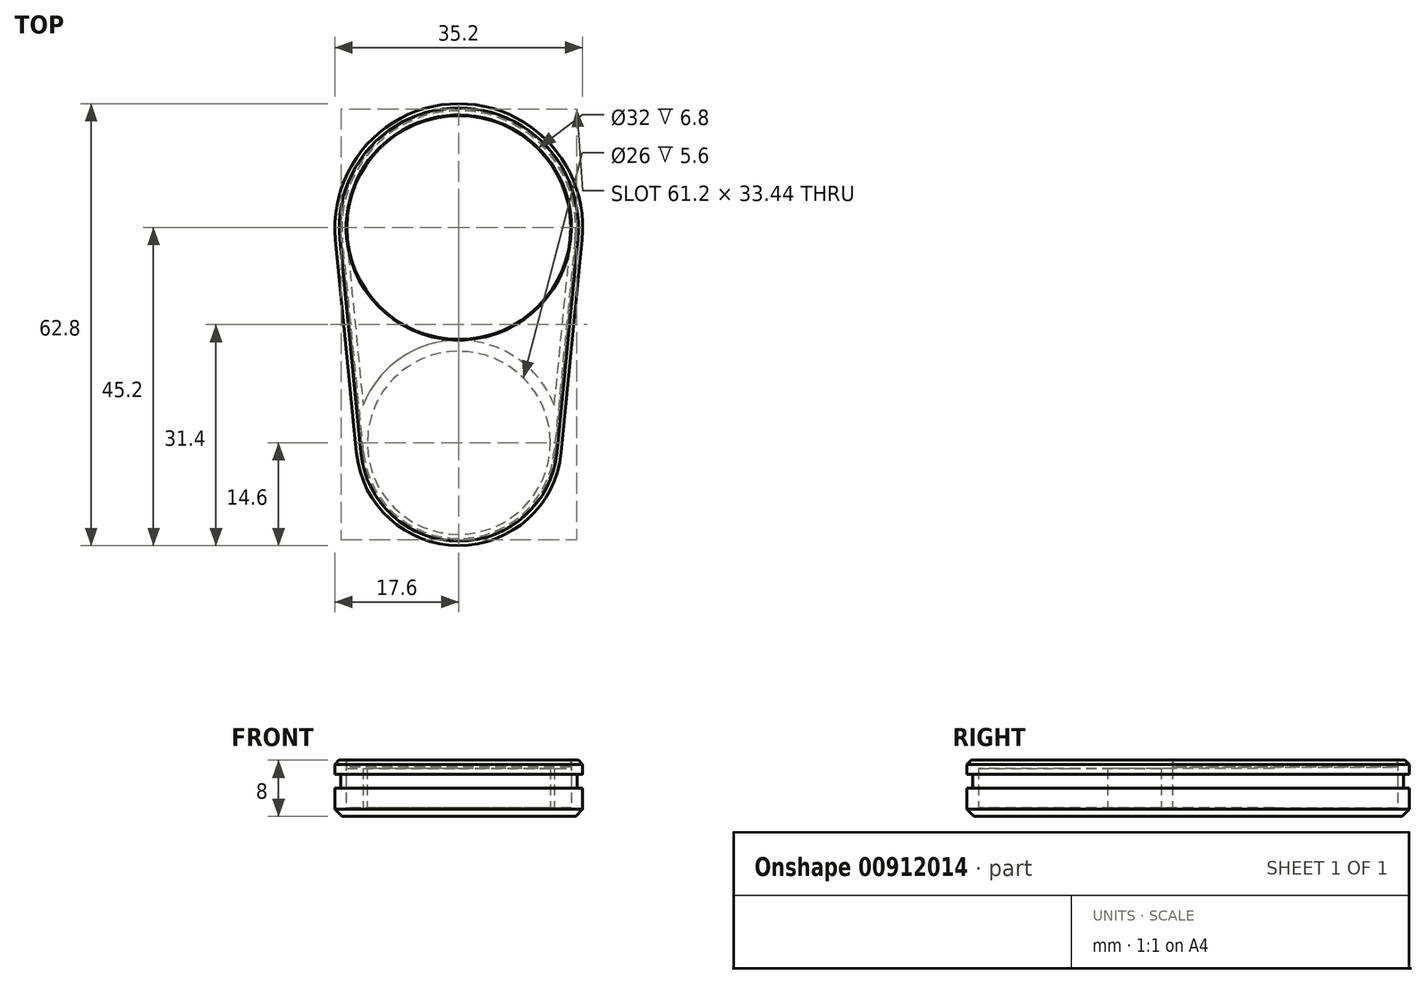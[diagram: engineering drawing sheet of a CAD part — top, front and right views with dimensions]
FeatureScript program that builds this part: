
annotation { "Feature Type Name" : "Feature", "Feature Type Description" : "" }
export const myFeature = defineFeature(function(context is Context, id is Id, definition is map)
    precondition{}
    {
        {
            var Q0;
            Q0=qCreatedBy(makeId("Top.planeOp"),FACE);
            var sketch = newSketch(context, id + "F0", { "sketchPlane" : qUnion([Q0])});
            skCircle(sketch, "E0", {"center": v(0, 0) * mm, "radius": 16 * mm});
            skCircle(sketch, "E1", {"center": v(0, 0) * mm, "radius": 17.6 * mm});
            skCircle(sketch, "E2", {"center": v(0, 0) * mm, "radius": 8.5 * mm});
            skCircle(sketch, "E3", {"center": v(0, 0) * mm, "radius": 7.3 * mm});
            skCircle(sketch, "E4", {"center": v(0, 0) * mm, "radius": 14 * mm});
            skLineSegment(sketch, "E5", {"start": v(0, 0) * mm, "end": v(0, -30.6) * mm, "construction": true});
            skCircle(sketch, "E6", {"center": v(0, -30.6) * mm, "radius": 13 * mm});
            skCircle(sketch, "E7", {"center": v(0, -30.6) * mm, "radius": 14.6 * mm});
            skLineSegment(sketch, "E8", {"start": v(14.53, -32.03) * mm, "end": v(17.69, 0) * mm});
            skLineSegment(sketch, "E9", {"start": v(-17.69, 0) * mm, "end": v(-14.53, -32.03) * mm});
            skLineSegment(sketch, "E10", {"start": v(-15.92, -1.57) * mm, "end": v(-12.94, -31.87) * mm});
            skLineSegment(sketch, "E11", {"start": v(12.94, -31.87) * mm, "end": v(15.92, -1.57) * mm});
            skSolve(sketch);
        }
        {
            var Q0;
            {var subQ0=sQuery(id+"F0.wireOp",EDGE,"E8");var subQ1=sQuery(id+"F0.wireOp",EDGE,"E1");var subQ2=makeQuery(id+"F0.imprint","INTERSECT",VERTEX,{"derivedFrom":[subQ1,subQ0]});Q0=makeQuery(id+"F0.imprint","IMPRINT",FACE,{"disambiguationData":[TD([[makeQuery(id+"F0.imprint","IMPRINT",EDGE,{"disambiguationData":[TD([[subQ2,1.0]])],"derivedFrom":subQ1}),-1.0]])]});}
            var Q1;
            {var subQ0=sQuery(id+"F0.wireOp",EDGE,"E7");var subQ1=sQuery(id+"F0.wireOp",EDGE,"E1");var subQ2=makeQuery(id+"F0.imprint","INTERSECT",VERTEX,{"disambiguationData":[OD(0.0)],"derivedFrom":[subQ1,subQ0]});Q1=makeQuery(id+"F0.imprint","IMPRINT",FACE,{"disambiguationData":[TD([[makeQuery(id+"F0.imprint","IMPRINT",EDGE,{"disambiguationData":[TD([[subQ2,-1.0]])],"derivedFrom":subQ1}),1.0]])]});}
            var Q2;
            {var subQ0=sQuery(id+"F0.wireOp",EDGE,"E11");var subQ1=sQuery(id+"F0.wireOp",EDGE,"E0");var subQ2=makeQuery(id+"F0.imprint","INTERSECT",VERTEX,{"derivedFrom":[subQ1,subQ0]});Q2=makeQuery(id+"F0.imprint","IMPRINT",FACE,{"disambiguationData":[TD([[makeQuery(id+"F0.imprint","IMPRINT",EDGE,{"disambiguationData":[TD([[subQ2,1.0]])],"derivedFrom":subQ1}),-1.0]])]});}
            var Q3;
            {var subQ5=sQuery(id+"F0.wireOp",EDGE,"E0");var subQ7=sQuery(id+"F0.wireOp",EDGE,"E10");var subQ9=makeQuery(id+"F0.imprint","INTERSECT",VERTEX,{"derivedFrom":[subQ5,subQ7]});Q3=makeQuery(id+"F0.imprint","IMPRINT",FACE,{"disambiguationData":[TD([[makeQuery(id+"F0.imprint","IMPRINT",EDGE,{"disambiguationData":[TD([[subQ9,1.0]])],"derivedFrom":subQ5}),-1.0]])]});}
            var Q4;
            {var subQ0=sQuery(id+"F0.wireOp",EDGE,"E10");var subQ1=sQuery(id+"F0.wireOp",EDGE,"E0");var subQ2=makeQuery(id+"F0.imprint","INTERSECT",VERTEX,{"derivedFrom":[subQ1,subQ0]});Q4=makeQuery(id+"F0.imprint","IMPRINT",FACE,{"disambiguationData":[TD([[makeQuery(id+"F0.imprint","IMPRINT",EDGE,{"disambiguationData":[TD([[subQ2,-1.0]])],"derivedFrom":subQ1}),-1.0]])]});}
            var Q5;
            {var subQ0=sQuery(id+"F0.wireOp",EDGE,"E6");var subQ1=makeQuery(id+"F0.imprint","INTERSECT",VERTEX,{"derivedFrom":[subQ0,sQuery(id+"F0.wireOp",EDGE,"E10")]});Q5=makeQuery(id+"F0.imprint","IMPRINT",FACE,{"disambiguationData":[TD([[makeQuery(id+"F0.imprint","IMPRINT",EDGE,{"disambiguationData":[TD([[subQ1,1.0]])],"derivedFrom":subQ0}),1.0]])]});}
            var Q6;
            {var subQ0=sQuery(id+"F0.wireOp",EDGE,"E7");var subQ1=sQuery(id+"F0.wireOp",EDGE,"E1");var subQ2=makeQuery(id+"F0.imprint","INTERSECT",VERTEX,{"disambiguationData":[OD(1.0)],"derivedFrom":[subQ1,subQ0]});Q6=makeQuery(id+"F0.imprint","IMPRINT",FACE,{"disambiguationData":[TD([[makeQuery(id+"F0.imprint","IMPRINT",EDGE,{"disambiguationData":[TD([[subQ2,-1.0]])],"derivedFrom":subQ1}),-1.0]])]});}
            var Q7;
            {var subQ0=sQuery(id+"F0.wireOp",EDGE,"E6");var subQ1=sQuery(id+"F0.wireOp",EDGE,"E1");var subQ2=makeQuery(id+"F0.imprint","INTERSECT",VERTEX,{"derivedFrom":[subQ1,subQ0]});Q7=makeQuery(id+"F0.imprint","IMPRINT",FACE,{"disambiguationData":[TD([[makeQuery(id+"F0.imprint","IMPRINT",EDGE,{"disambiguationData":[TD([[subQ2,-1.0]])],"derivedFrom":subQ1}),-1.0]])]});}
            var Q8;
            {var subQ0=sQuery(id+"F0.wireOp",EDGE,"E9");var subQ1=sQuery(id+"F0.wireOp",EDGE,"E1");var subQ2=makeQuery(id+"F0.imprint","INTERSECT",VERTEX,{"derivedFrom":[subQ1,subQ0]});Q8=makeQuery(id+"F0.imprint","IMPRINT",FACE,{"disambiguationData":[TD([[makeQuery(id+"F0.imprint","IMPRINT",EDGE,{"disambiguationData":[TD([[subQ2,-1.0]])],"derivedFrom":subQ1}),-1.0]])]});}
            var Q9;
            {var subQ0=sQuery(id+"F0.wireOp",EDGE,"E7");var subQ1=sQuery(id+"F0.wireOp",EDGE,"E1");var subQ2=makeQuery(id+"F0.imprint","INTERSECT",VERTEX,{"disambiguationData":[OD(0.0)],"derivedFrom":[subQ1,subQ0]});Q9=makeQuery(id+"F0.imprint","IMPRINT",FACE,{"disambiguationData":[TD([[makeQuery(id+"F0.imprint","IMPRINT",EDGE,{"disambiguationData":[TD([[subQ2,-1.0]])],"derivedFrom":subQ1}),-1.0]])]});}
            var Q10;
            {var subQ0=sQuery(id+"F0.wireOp",EDGE,"E10");var subQ1=sQuery(id+"F0.wireOp",EDGE,"E1");var subQ2=makeQuery(id+"F0.imprint","INTERSECT",VERTEX,{"derivedFrom":[subQ1,subQ0]});Q10=makeQuery(id+"F0.imprint","IMPRINT",FACE,{"disambiguationData":[TD([[makeQuery(id+"F0.imprint","IMPRINT",EDGE,{"disambiguationData":[TD([[subQ2,-1.0]])],"derivedFrom":subQ1}),-1.0]])]});}
            var Q11;
            {var subQ5=sQuery(id+"F0.wireOp",EDGE,"E10");var subQ7=sQuery(id+"F0.wireOp",EDGE,"E6");var subQ8=makeQuery(id+"F0.imprint","INTERSECT",VERTEX,{"derivedFrom":[subQ7,subQ5]});Q11=makeQuery(id+"F0.imprint","IMPRINT",FACE,{"disambiguationData":[TD([[makeQuery(id+"F0.imprint","IMPRINT",EDGE,{"disambiguationData":[TD([[subQ8,-1.0]])],"derivedFrom":subQ7}),-1.0]])]});}
            extrude(context, id + "F1", {"entities" : qUnion([Q0, Q1, Q2, Q3, Q4, Q5, Q6, Q7, Q8, Q9, Q10, Q11]), "depth" : 4 * mm, "offsetDistance" : 25 * mm});
        }
        {
            var Q0;
            {var subQ0=sQuery(id+"F0.wireOp",EDGE,"E6");var subQ1=makeQuery(id+"F0.imprint","INTERSECT",VERTEX,{"derivedFrom":[subQ0,sQuery(id+"F0.wireOp",EDGE,"E10")]});Q0=makeQuery(id+"F0.imprint","IMPRINT",FACE,{"disambiguationData":[TD([[makeQuery(id+"F0.imprint","IMPRINT",EDGE,{"disambiguationData":[TD([[subQ1,1.0]])],"derivedFrom":subQ0}),1.0]])]});}
            var Q1;
            {var subQ0=sQuery(id+"F0.wireOp",EDGE,"E10");var subQ1=sQuery(id+"F0.wireOp",EDGE,"E1");var subQ2=makeQuery(id+"F0.imprint","INTERSECT",VERTEX,{"derivedFrom":[subQ1,subQ0]});Q1=makeQuery(id+"F0.imprint","IMPRINT",FACE,{"disambiguationData":[TD([[makeQuery(id+"F0.imprint","IMPRINT",EDGE,{"disambiguationData":[TD([[subQ2,-1.0]])],"derivedFrom":subQ1}),-1.0]])]});}
            var Q2;
            {var subQ0=sQuery(id+"F0.wireOp",EDGE,"E7");var subQ1=sQuery(id+"F0.wireOp",EDGE,"E1");var subQ2=makeQuery(id+"F0.imprint","INTERSECT",VERTEX,{"disambiguationData":[OD(1.0)],"derivedFrom":[subQ1,subQ0]});Q2=makeQuery(id+"F0.imprint","IMPRINT",FACE,{"disambiguationData":[TD([[makeQuery(id+"F0.imprint","IMPRINT",EDGE,{"disambiguationData":[TD([[subQ2,-1.0]])],"derivedFrom":subQ1}),-1.0]])]});}
            var Q3;
            {var subQ0=sQuery(id+"F0.wireOp",EDGE,"E10");var subQ1=sQuery(id+"F0.wireOp",EDGE,"E0");var subQ2=makeQuery(id+"F0.imprint","INTERSECT",VERTEX,{"derivedFrom":[subQ1,subQ0]});Q3=makeQuery(id+"F0.imprint","IMPRINT",FACE,{"disambiguationData":[TD([[makeQuery(id+"F0.imprint","IMPRINT",EDGE,{"disambiguationData":[TD([[subQ2,-1.0]])],"derivedFrom":subQ1}),-1.0]])]});}
            var Q4;
            {var subQ0=sQuery(id+"F0.wireOp",EDGE,"E11");var subQ1=sQuery(id+"F0.wireOp",EDGE,"E0");var subQ2=makeQuery(id+"F0.imprint","INTERSECT",VERTEX,{"derivedFrom":[subQ1,subQ0]});Q4=makeQuery(id+"F0.imprint","IMPRINT",FACE,{"disambiguationData":[TD([[makeQuery(id+"F0.imprint","IMPRINT",EDGE,{"disambiguationData":[TD([[subQ2,1.0]])],"derivedFrom":subQ1}),-1.0]])]});}
            extrude(context, id + "F2", {"entities" : qUnion([Q0, Q1, Q2, Q3, Q4]), "operationType" : NewBodyOperationType.REMOVE, "depth" : 2.8 * mm, "offsetDistance" : 25 * mm});
        }
        {
            var Q0;
            Q0=makeQuery(id+"F1.opExtrude","CAP_EDGE",EDGE,{"disambiguationData":[OSD([sQuery(id+"F0.wireOp",EDGE,"E7")])],"isStart":false});
            var Q1;
            Q1=makeQuery(id+"F1.opExtrude","CAP_EDGE",EDGE,{"disambiguationData":[OSD([sQuery(id+"F0.wireOp",EDGE,"E8")])],"isStart":false});
            var Q2;
            Q2=makeQuery(id+"F1.opExtrude","CAP_EDGE",EDGE,{"disambiguationData":[OSD([sQuery(id+"F0.wireOp",EDGE,"E1")])],"isStart":false});
            var Q3;
            Q3=makeQuery(id+"F1.opExtrude","CAP_EDGE",EDGE,{"disambiguationData":[OSD([sQuery(id+"F0.wireOp",EDGE,"E9")])],"isStart":false});
            chamfer(context, id + "F3", {"entities" : qUnion([Q0, Q1, Q2, Q3]), "width" : 0.6 * mm, "tangentPropagation" : true});
        }
        {
            var Q0;
            Q0 = qSketchRegion(id + "F0", true);
            var Q1;
            Q1=makeQuery(id+"F0.imprint","IMPRINT",FACE,{"disambiguationData":[TD([[makeQuery(id+"F0.imprint","IMPRINT",EDGE,{"derivedFrom":sQuery(id+"F0.wireOp",EDGE,"E2")}),-1.0]])]});
            var Q2;
            Q2=makeQuery(id+"F0.imprint","IMPRINT",FACE,{"disambiguationData":[TD([[makeQuery(id+"F0.imprint","IMPRINT",EDGE,{"derivedFrom":sQuery(id+"F0.wireOp",EDGE,"E2")}),1.0]])]});
            var Q3;
            Q3=makeQuery(id+"F0.imprint","IMPRINT",FACE,{"disambiguationData":[TD([[makeQuery(id+"F0.imprint","IMPRINT",EDGE,{"derivedFrom":sQuery(id+"F0.wireOp",EDGE,"E3")}),1.0]])]});
            var Q4;
            Q4=makeQuery(id+"F0.imprint","IMPRINT",FACE,{"disambiguationData":[TD([[makeQuery(id+"F0.imprint","IMPRINT",EDGE,{"derivedFrom":sQuery(id+"F0.wireOp",EDGE,"E4")}),-1.0]])]});
            var Q5;
            {var subQ0=sQuery(id+"F0.wireOp",EDGE,"E10");var subQ1=sQuery(id+"F0.wireOp",EDGE,"E0");var subQ2=makeQuery(id+"F0.imprint","INTERSECT",VERTEX,{"derivedFrom":[subQ1,subQ0]});Q5=makeQuery(id+"F0.imprint","IMPRINT",FACE,{"disambiguationData":[TD([[makeQuery(id+"F0.imprint","IMPRINT",EDGE,{"disambiguationData":[TD([[subQ2,-1.0]])],"derivedFrom":subQ1}),-1.0]])]});}
            var Q6;
            {var subQ0=sQuery(id+"F0.wireOp",EDGE,"E10");var subQ1=sQuery(id+"F0.wireOp",EDGE,"E1");var subQ2=makeQuery(id+"F0.imprint","INTERSECT",VERTEX,{"derivedFrom":[subQ1,subQ0]});Q6=makeQuery(id+"F0.imprint","IMPRINT",FACE,{"disambiguationData":[TD([[makeQuery(id+"F0.imprint","IMPRINT",EDGE,{"disambiguationData":[TD([[subQ2,-1.0]])],"derivedFrom":subQ1}),-1.0]])]});}
            var Q7;
            {var subQ0=sQuery(id+"F0.wireOp",EDGE,"E7");var subQ1=sQuery(id+"F0.wireOp",EDGE,"E1");var subQ2=makeQuery(id+"F0.imprint","INTERSECT",VERTEX,{"disambiguationData":[OD(1.0)],"derivedFrom":[subQ1,subQ0]});Q7=makeQuery(id+"F0.imprint","IMPRINT",FACE,{"disambiguationData":[TD([[makeQuery(id+"F0.imprint","IMPRINT",EDGE,{"disambiguationData":[TD([[subQ2,-1.0]])],"derivedFrom":subQ1}),-1.0]])]});}
            var Q8;
            {var subQ0=sQuery(id+"F0.wireOp",EDGE,"E6");var subQ1=sQuery(id+"F0.wireOp",EDGE,"E1");var subQ2=makeQuery(id+"F0.imprint","INTERSECT",VERTEX,{"derivedFrom":[subQ1,subQ0]});Q8=makeQuery(id+"F0.imprint","IMPRINT",FACE,{"disambiguationData":[TD([[makeQuery(id+"F0.imprint","IMPRINT",EDGE,{"disambiguationData":[TD([[subQ2,-1.0]])],"derivedFrom":subQ1}),-1.0]])]});}
            var Q9;
            {var subQ0=sQuery(id+"F0.wireOp",EDGE,"E11");var subQ1=sQuery(id+"F0.wireOp",EDGE,"E0");var subQ2=makeQuery(id+"F0.imprint","INTERSECT",VERTEX,{"derivedFrom":[subQ1,subQ0]});Q9=makeQuery(id+"F0.imprint","IMPRINT",FACE,{"disambiguationData":[TD([[makeQuery(id+"F0.imprint","IMPRINT",EDGE,{"disambiguationData":[TD([[subQ2,1.0]])],"derivedFrom":subQ1}),-1.0]])]});}
            var Q10;
            {var subQ0=sQuery(id+"F0.wireOp",EDGE,"E7");var subQ1=sQuery(id+"F0.wireOp",EDGE,"E1");var subQ2=makeQuery(id+"F0.imprint","INTERSECT",VERTEX,{"disambiguationData":[OD(0.0)],"derivedFrom":[subQ1,subQ0]});Q10=makeQuery(id+"F0.imprint","IMPRINT",FACE,{"disambiguationData":[TD([[makeQuery(id+"F0.imprint","IMPRINT",EDGE,{"disambiguationData":[TD([[subQ2,-1.0]])],"derivedFrom":subQ1}),1.0]])]});}
            var Q11;
            {var subQ0=sQuery(id+"F0.wireOp",EDGE,"E7");var subQ1=sQuery(id+"F0.wireOp",EDGE,"E1");var subQ2=makeQuery(id+"F0.imprint","INTERSECT",VERTEX,{"disambiguationData":[OD(0.0)],"derivedFrom":[subQ1,subQ0]});Q11=makeQuery(id+"F0.imprint","IMPRINT",FACE,{"disambiguationData":[TD([[makeQuery(id+"F0.imprint","IMPRINT",EDGE,{"disambiguationData":[TD([[subQ2,-1.0]])],"derivedFrom":subQ1}),-1.0]])]});}
            var Q12;
            {var subQ0=sQuery(id+"F0.wireOp",EDGE,"E6");var subQ1=makeQuery(id+"F0.imprint","INTERSECT",VERTEX,{"derivedFrom":[subQ0,sQuery(id+"F0.wireOp",EDGE,"E10")]});Q12=makeQuery(id+"F0.imprint","IMPRINT",FACE,{"disambiguationData":[TD([[makeQuery(id+"F0.imprint","IMPRINT",EDGE,{"disambiguationData":[TD([[subQ1,1.0]])],"derivedFrom":subQ0}),1.0]])]});}
            extrude(context, id + "F4", {"entities" : qUnion([Q0, Q1, Q2, Q3, Q4, Q5, Q6, Q7, Q8, Q9, Q10, Q11, Q12]), "oppositeDirection" : true, "depth" : 4 * mm, "offsetDistance" : 25 * mm});
        }
        {
            var Q0;
            {var subQ0=sQuery(id+"F0.wireOp",EDGE,"E6");var subQ1=makeQuery(id+"F0.imprint","INTERSECT",VERTEX,{"derivedFrom":[subQ0,sQuery(id+"F0.wireOp",EDGE,"E10")]});Q0=makeQuery(id+"F0.imprint","IMPRINT",FACE,{"disambiguationData":[TD([[makeQuery(id+"F0.imprint","IMPRINT",EDGE,{"disambiguationData":[TD([[subQ1,1.0]])],"derivedFrom":subQ0}),1.0]])]});}
            extrude(context, id + "F5", {"entities" : qUnion([Q0]), "operationType" : NewBodyOperationType.REMOVE, "oppositeDirection" : true, "depth" : 2.8 * mm, "offsetDistance" : 25 * mm});
        }
        {
            var Q0;
            {var subQ0=sQuery(id+"F0.wireOp",EDGE,"E7");var subQ1=sQuery(id+"F0.wireOp",EDGE,"E1");var subQ2=makeQuery(id+"F0.imprint","INTERSECT",VERTEX,{"disambiguationData":[OD(1.0)],"derivedFrom":[subQ1,subQ0]});Q0=makeQuery(id+"F0.imprint","IMPRINT",FACE,{"disambiguationData":[TD([[makeQuery(id+"F0.imprint","IMPRINT",EDGE,{"disambiguationData":[TD([[subQ2,-1.0]])],"derivedFrom":subQ1}),-1.0]])]});}
            var Q1;
            {var subQ0=sQuery(id+"F0.wireOp",EDGE,"E11");var subQ1=sQuery(id+"F0.wireOp",EDGE,"E0");var subQ2=makeQuery(id+"F0.imprint","INTERSECT",VERTEX,{"derivedFrom":[subQ1,subQ0]});Q1=makeQuery(id+"F0.imprint","IMPRINT",FACE,{"disambiguationData":[TD([[makeQuery(id+"F0.imprint","IMPRINT",EDGE,{"disambiguationData":[TD([[subQ2,1.0]])],"derivedFrom":subQ1}),-1.0]])]});}
            var Q2;
            Q2=makeQuery(id+"F0.imprint","IMPRINT",FACE,{"disambiguationData":[TD([[makeQuery(id+"F0.imprint","IMPRINT",EDGE,{"derivedFrom":sQuery(id+"F0.wireOp",EDGE,"E4")}),-1.0]])]});
            var Q3;
            Q3=makeQuery(id+"F0.imprint","IMPRINT",FACE,{"disambiguationData":[TD([[makeQuery(id+"F0.imprint","IMPRINT",EDGE,{"derivedFrom":sQuery(id+"F0.wireOp",EDGE,"E2")}),-1.0]])]});
            var Q4;
            Q4=makeQuery(id+"F0.imprint","IMPRINT",FACE,{"disambiguationData":[TD([[makeQuery(id+"F0.imprint","IMPRINT",EDGE,{"derivedFrom":sQuery(id+"F0.wireOp",EDGE,"E3")}),1.0]])]});
            var Q5;
            Q5=makeQuery(id+"F0.imprint","IMPRINT",FACE,{"disambiguationData":[TD([[makeQuery(id+"F0.imprint","IMPRINT",EDGE,{"derivedFrom":sQuery(id+"F0.wireOp",EDGE,"E2")}),1.0]])]});
            var Q6;
            {var subQ0=sQuery(id+"F0.wireOp",EDGE,"E10");var subQ1=sQuery(id+"F0.wireOp",EDGE,"E0");var subQ2=makeQuery(id+"F0.imprint","INTERSECT",VERTEX,{"derivedFrom":[subQ1,subQ0]});Q6=makeQuery(id+"F0.imprint","IMPRINT",FACE,{"disambiguationData":[TD([[makeQuery(id+"F0.imprint","IMPRINT",EDGE,{"disambiguationData":[TD([[subQ2,-1.0]])],"derivedFrom":subQ1}),-1.0]])]});}
            var Q7;
            {var subQ0=sQuery(id+"F0.wireOp",EDGE,"E10");var subQ1=sQuery(id+"F0.wireOp",EDGE,"E1");var subQ2=makeQuery(id+"F0.imprint","INTERSECT",VERTEX,{"derivedFrom":[subQ1,subQ0]});Q7=makeQuery(id+"F0.imprint","IMPRINT",FACE,{"disambiguationData":[TD([[makeQuery(id+"F0.imprint","IMPRINT",EDGE,{"disambiguationData":[TD([[subQ2,-1.0]])],"derivedFrom":subQ1}),-1.0]])]});}
            extrude(context, id + "F6", {"entities" : qUnion([Q0, Q1, Q2, Q3, Q4, Q5, Q6, Q7]), "operationType" : NewBodyOperationType.REMOVE, "oppositeDirection" : true, "depth" : 2.8 * mm, "offsetDistance" : 25 * mm});
        }
        {
            var Q0;
            Q0=makeQuery(id+"F4.opExtrude","CAP_EDGE",EDGE,{"disambiguationData":[OSD([sQuery(id+"F0.wireOp",EDGE,"E9")])],"isStart":false});
            var Q1;
            Q1=makeQuery(id+"F4.opExtrude","CAP_EDGE",EDGE,{"disambiguationData":[OSD([sQuery(id+"F0.wireOp",EDGE,"E1")])],"isStart":false});
            var Q2;
            Q2=makeQuery(id+"F4.opExtrude","CAP_EDGE",EDGE,{"disambiguationData":[OSD([sQuery(id+"F0.wireOp",EDGE,"E8")])],"isStart":false});
            var Q3;
            Q3=makeQuery(id+"F4.opExtrude","CAP_EDGE",EDGE,{"disambiguationData":[OSD([sQuery(id+"F0.wireOp",EDGE,"E7")])],"isStart":false});
            chamfer(context, id + "F7", {"entities" : qUnion([Q0, Q1, Q2, Q3]), "width" : 1 * mm, "tangentPropagation" : true});
        }
        {
            var Q0;
            Q0=makeQuery(id+"F6.boolean.opBoolean","COPY",EDGE,{"derivedFrom":makeQuery(id+"F6.opExtrude","SWEPT_EDGE",EDGE,{"disambiguationData":[OSD([sQuery(id+"F0.wireOp",EDGE,"E7"),sQuery(id+"F0.wireOp",EDGE,"E11")])]})});
            var Q1;
            Q1=makeQuery(id+"F6.boolean.opBoolean","COPY",EDGE,{"derivedFrom":makeQuery(id+"F6.opExtrude","SWEPT_EDGE",EDGE,{"disambiguationData":[OSD([sQuery(id+"F0.wireOp",EDGE,"E7"),sQuery(id+"F0.wireOp",EDGE,"E10")])]})});
            cPlane(context, id + "F8", {"entities" : qUnion([Q0, Q1]), "cplaneType" : CPlaneType.LINE_ANGLE, "offset" : 25 * mm, "angle" : 0 * degree, "width" : 150 * mm, "height" : 150 * mm});
        }
        {
            var Q0;
            Q0=makeQuery(id+"F1.opExtrude","CAP_FACE",FACE,{"disambiguationData":[OSD([sQuery(id+"F0.wireOp",EDGE,"E0"),sQuery(id+"F0.wireOp",EDGE,"E1"),sQuery(id+"F0.wireOp",EDGE,"E7"),sQuery(id+"F0.wireOp",EDGE,"E8"),sQuery(id+"F0.wireOp",EDGE,"E9")])],"isStart":false});
            var sketch = newSketch(context, id + "F9", { "sketchPlane" : qUnion([Q0])});
            skCircle(sketch, "E12", {"center": v(0, 0) * mm, "radius": 15.9 * mm});
            skSolve(sketch);
        }
        {
            var Q0;
            Q0=makeQuery(id+"F9.imprint","IMPRINT",FACE,{"disambiguationData":[TD([[makeQuery(id+"F9.imprint","IMPRINT",EDGE,{"derivedFrom":sQuery(id+"F9.wireOp",EDGE,"E12")}),1.0]])]});
            var Q1;
            Q1=sQuery(id+"F9.wireOp",EDGE,"E12");
            extrude(context, id + "F10", {"entities" : qUnion([Q0]), "surfaceEntities" : qUnion([Q1]), "oppositeDirection" : true, "depth" : 1 * mm, "offsetDistance" : 25 * mm});
        }
        {
            var Q0;
            Q0=makeQuery(id+"F4.opExtrude","CAP_FACE",FACE,{"disambiguationData":[OSD([sQuery(id+"F0.wireOp",EDGE,"E1"),sQuery(id+"F0.wireOp",EDGE,"E7"),sQuery(id+"F0.wireOp",EDGE,"E8"),sQuery(id+"F0.wireOp",EDGE,"E9")])],"isStart":true});
            var sketch = newSketch(context, id + "F11", { "sketchPlane" : qUnion([Q0])});
            skCircle(sketch, "E13.0", {"center": v(0, -30.6) * mm, "radius": 13.8 * mm});
            skArc(sketch, "E14.0", {"start": v(13.73, -31.95) * mm, "mid": v(0, -16.8) * mm, "end": v(-13.73, -31.95) * mm});
            skLineSegment(sketch, "E14.1", {"start": v(13.73, -31.95) * mm, "end": v(16.72, -1.65) * mm});
            skArc(sketch, "E14.2", {"start": v(16.72, -1.65) * mm, "mid": v(0, 16.8) * mm, "end": v(-16.72, -1.65) * mm});
            skLineSegment(sketch, "E14.3", {"start": v(-16.72, -1.65) * mm, "end": v(-13.73, -31.95) * mm});
            skLineSegment(sketch, "E15", {"start": v(13.59, -25.26) * mm, "end": v(12.94, -31.87) * mm});
            skLineSegment(sketch, "E16", {"start": v(-13.59, -25.26) * mm, "end": v(-12.94, -31.87) * mm});
            skSolve(sketch);
        }
        {
            var Q0;
            {var subQ1=sQuery(id+"F11.wireOp",EDGE,"E14.1");Q0=makeQuery(id+"F11.imprint","IMPRINT",FACE,{"disambiguationData":[TD([[makeQuery(id+"F11.imprint","IMPRINT",EDGE,{"derivedFrom":subQ1}),-1.0]])]});}
            extrude(context, id + "F12", {"entities" : qUnion([Q0]), "operationType" : NewBodyOperationType.ADD, "depth" : 2 * mm, "offsetDistance" : 25 * mm});
        }
        {
            var Q0;
            {var subQ1=sQuery(id+"F11.wireOp",EDGE,"E14.1");Q0=makeQuery(id+"F11.imprint","IMPRINT",FACE,{"disambiguationData":[TD([[makeQuery(id+"F11.imprint","IMPRINT",EDGE,{"derivedFrom":subQ1}),-1.0]])]});}
            extrude(context, id + "F13", {"entities" : qUnion([Q0]), "operationType" : NewBodyOperationType.REMOVE, "depth" : 2 * mm, "offsetDistance" : 25 * mm});
        }
    });
